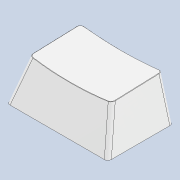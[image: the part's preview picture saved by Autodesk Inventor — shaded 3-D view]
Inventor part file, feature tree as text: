
AUTODESK INVENTOR PART (.ipt)
format: ipt  version: 2021 (Build 250183000, 183)  size: 237,568 bytes
history: native  units: in
note: dims shown in document units (in); Inventor stores cm internally (conversion verified against a paired STEP export)
features: chamfer x1
ambient origin geometry x8: Origin, YZ Plane, XZ Plane, XY Plane, X Axis, Y Axis, Z Axis, Center Point
bodies: Solid1 (feature_tree)
feature tree (1):
  chamfer  "Chamfer1"  [1 undecoded]
note: 1 required parameter value undecoded (feature->parameter linkage not recoverable at this tier; creation-order binding heuristic only, values carry confidence <= 0.55)
